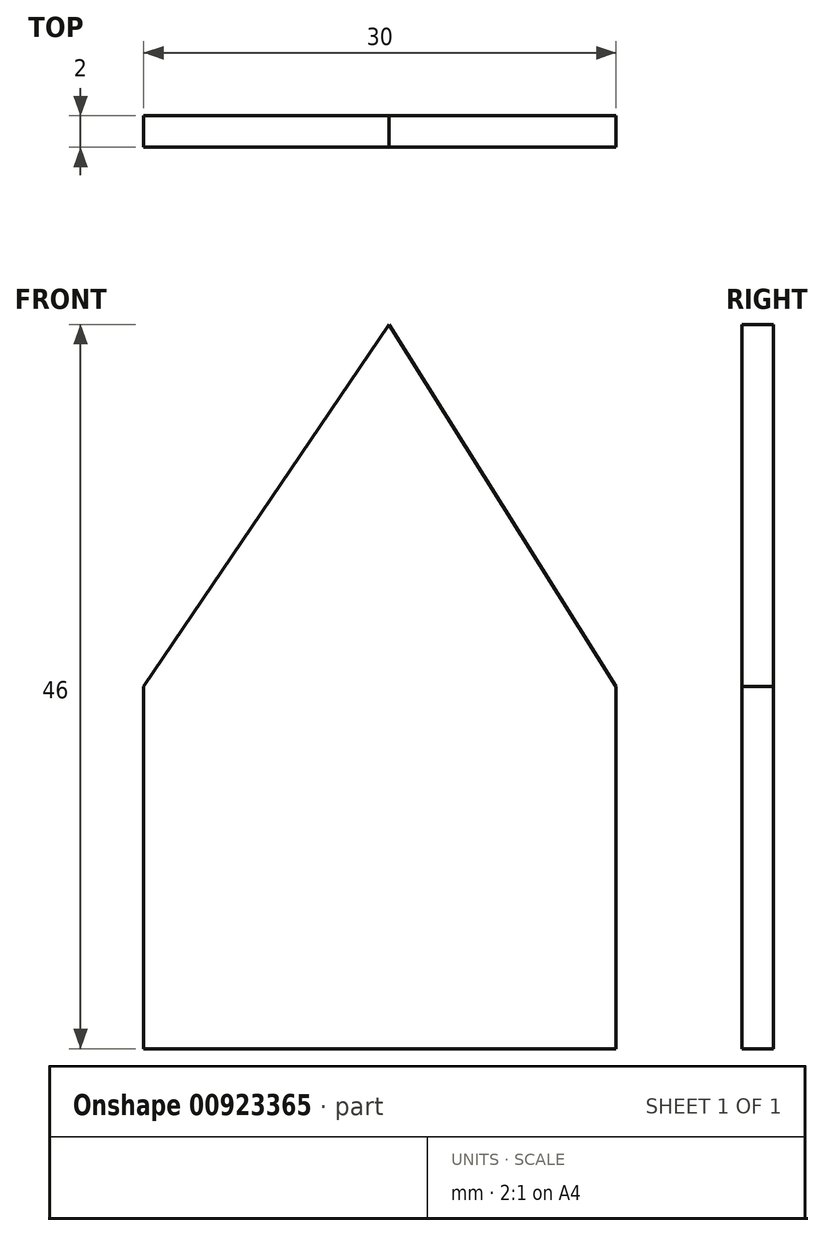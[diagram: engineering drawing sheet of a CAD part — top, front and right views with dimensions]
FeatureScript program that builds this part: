
annotation { "Feature Type Name" : "Feature", "Feature Type Description" : "" }
export const myFeature = defineFeature(function(context is Context, id is Id, definition is map)
    precondition{}
    {
        {
            var Q0;
            Q0=qCreatedBy(makeId("Front.planeOp"),FACE);
            var sketch = newSketch(context, id + "F0", { "sketchPlane" : qUnion([Q0])});
            skLineSegment(sketch, "E0.top", {"start": v(-56.92, -48) * mm, "end": v(-26.92, -48) * mm});
            skLineSegment(sketch, "E1", {"start": v(-41.35, -2) * mm, "end": v(-56.92, -25) * mm});
            skLineSegment(sketch, "E2", {"start": v(-56.92, -25) * mm, "end": v(-41.35, -2) * mm});
            skLineSegment(sketch, "E3", {"start": v(-26.92, -25) * mm, "end": v(-41.35, -2) * mm});
            skLineSegment(sketch, "E4", {"start": v(-56.92, -25) * mm, "end": v(-56.92, -48) * mm});
            skLineSegment(sketch, "E5", {"start": v(-26.92, -25) * mm, "end": v(-26.92, -48) * mm});
            skSolve(sketch);
        }
        {
            var Q0;
            Q0 = qSketchRegion(id + "F0", true);
            extrude(context, id + "F1", {"entities" : qUnion([Q0]), "depth" : 2 * mm, "offsetDistance" : 25 * mm});
        }
    });
